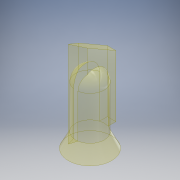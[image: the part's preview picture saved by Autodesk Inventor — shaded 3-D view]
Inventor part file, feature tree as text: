
AUTODESK INVENTOR PART (.ipt)
format: ipt  version: 2017 (Build 210142000, 142)  size: 143,872 bytes
history: native  units: mm
features: sketch x6, plane x3, extrude x3, loft x1, revolve x1
ambient origin geometry x8: Origin, YZ Plane, XZ Plane, XY Plane, X Axis, Y Axis, Z Axis, Center Point
bodies: Body1 (feature_tree)
feature tree (14):
  sketch  "Sketch1"  dims[d0=15.0mm d4=10.0mm]
  plane  "Work Plane1"
  loft  "Loft1"
  extrude  "Extrusion2"  TaperAngle=0.0deg  [1 undecoded]
  revolve  "Revolution1"  [1 undecoded]
  plane  "Work Plane2"
  extrude  "Extrusion3"  [1 undecoded]
  plane  "Work Plane3"
  extrude  "Extrusion4"  Depth=3.0mm TaperAngle=0.0deg
  sketch  "Sketch2"  dims[d5=0.0mm d6=90.0deg d7=0.0mm d8=90.0deg]
  sketch  "Sketch3"  dims[d9=10.0mm d10=15.0mm d11=0.0mm]
  sketch  "Sketch4"  dims[d12=180.0deg d13=-5.0mm]
  sketch  "Sketch6"  dims[d14=3.0mm d16=30.0mm d17=0.0mm]
  sketch  "Sketch7"  dims[d18=30.0deg d19=23.462241mm d20=7.5mm d21=0.0mm]
note: 3 required parameter values undecoded (feature->parameter linkage not recoverable at this tier; creation-order binding heuristic only, values carry confidence <= 0.55)